# Revit family: IS_Conca_T3971_BIM_IT
name_source: partatom
category: Plumbing Fixtures
revit_build: Autodesk Revit 2017 (Build: 20160225_1515(x64)
units: mm (PartAtom-declared; Revit-internal decimal feet)

## family parameters
Always vertical = No
Cut with Voids When Loaded = No
OmniClass Number = 23.45.05.14.21.11
OmniClass Title = Bath/Shower Units
Part Type = Normal
Room Calculation Point = No
Round Connector Dimension = Use Diameter
Shared = No
Work Plane-Based = No

## types (3) — shared parameters
BIMobject category = Storage
BIMobject category code = sanitary-storage
BIMobject main category = Sanitary
BIMobject main category code = sanitary
Installation instructions = https://www.idealspec.co.uk
Maniglia = No
Manufacturer = Ideal Standard
NominalDepth = 505 mm  [stored 1.65682 ft]
NominalHeight = 6 mm  [stored 0.019685 ft]
NominalWidth = 1001 mm  [stored 3.28412 ft]
PiattoDoccia = No
Product group = Bathroom_Furniture
URL = https://www.ideal-standard.co.uk
Uniclass 2015 Code = Pr_40_30_78_03
Uniclass 2015 Name = Bathroom cabinets
zero-valued in all types: CostoDiSostituzione, DimensioneScarico, LunghezzaNominale, Nominal depth, Nominal height, SeatMaterial, SpessoreDelMateriale, SpilloverLivello, Weight Net (Kg)

## per-type parameters (varying)
- T3971DG - Conca CERAMIC WTOP 100 X 50.5  CM BLM - T3971 - DG: AltezzaNominale=0 mm  [stored 0 ft]; Description=Porcelain stoneware countertop,   1200 x 505 x 6 mm . Compact, hard non-porous colored ceramic with high resistance to mechanical stress, chemical attack, scratches and abrasion. It is easy to clean. To be combined with vanity units without countertop.Black Marble finish.; LarghezzaNominale=0 mm  [stored 0 ft]; Model=T3971DG; ProfonditaNominale=0 mm  [stored 0 ft]
- T3971DH - Conca CERAMIC WTOP 100 X 50.5  CM BLM - T3971 - DH: AltezzaNominale=0 mm  [stored 0 ft]; Description=Porcelain stoneware countertop,   1200 x 505 x 6 mm . Compact, hard non-porous colored ceramic with high resistance to mechanical stress, chemical attack, scratches and abrasion. It is easy to clean. To be combined with vanity units without countertop.Black Marble finish.; LarghezzaNominale=0 mm  [stored 0 ft]; Model=T3971DG; ProfonditaNominale=0 mm  [stored 0 ft]
- T3971DI - Conca CERAMIC WTOP 100 X 50.5  CM BLM - T3971 - DI: Accessori=https://www.idealstandard.it; Aiuto=https://www.idealstandard.it; AltezzaNominale=6 mm  [stored 0.019685 ft]; Autore=Ideal Standard; Brand=https://www.idealstandard.it; Caratteristiche=Piano da appogio in gres porcellanato  1200 x 505 x 6 mm  Il gres porcellanato è una ceramica a pasta compatta e dura colorata non porosa un'elevata resistenza alle sollecitazioni meccaniche, agli attacchi chimici, ai graffi e all'abrasione. Si pulisce con estrema facilità. Da abbinare ai mobili sottolavabo senza piano da appoggio.Finitura Marmo nero lucido; CodiceABarre=8014140461951; CodiceArticolo=T3971DI; Colore=Black Marble finish.; Description=Porcelain stoneware countertop,   1200 x 505 x 6 mm . Compact, hard non-porous colored ceramic with high resistance to mechanical stress, chemical attack, scratches and abrasion. It is easy to clean. To be combined with vanity units without countertop. Polished black marble finish; DescrizioneClassifcazioneUni2015=Bathroom cabinets; Desrizione=Piano da appogio in gres porcellanato  1200 x 505 x 6 mm  Il gres porcellanato è una ceramica a pasta compatta e dura colorata non porosa un'elevata resistenza alle sollecitazioni meccaniche, agli attacchi chimici, ai graffi e all'abrasione. Si pulisce con estrema facilità. Da abbinare ai mobili sottolavabo senza piano da appoggio.Finitura Marmo nero lucido; DurataGaranzia=2; DurataGaranziaProdotti=2; Finitura=Black Marble finish.; Forma=Rettangolare; Garanzia=Garanzia Idealstandard; IfcEsportaCome=IfcFurnitureType; InformaziniGaranzia=https://www.idealstandard.it; InformazioniDiProdotto=http://www.idealstandard.it; InformazioniGaranzia=https://www.idealstandard.it; InstruzioniInstallazione=https://www.idealstandard.it; LarghezzaNominale=1003 mm; Materiale=Ceramics; Model=T3971DI; ModelloDiRiferimento=T3971DI; Nome=BathroomCabinets_Conca_T3971DI_IdealStandard; NomeOggettoBim=ISI_IdealStandard_Bathroom Cabinets_Conca_T3971DI; NumeroDiModello=T3971DI; PesoNetto=7; Produttore=Ideal Standard; ProfonditaNominale=505 mm  [stored 1.65682 ft]; Revisione=1; RiferimentoClassificazioneUni2015=Pr_40_30_78_03; Spazio=Interno; Telefono=800 652 290; TipoEspotazioneIfc=Bathroom cabinets; UnitàDurata=Anno; UnitàDurataGaranzia=Anno; UnitàLineare=Milimitre; UnitàMonetaria=€; UnitàSuperficie=Milimitre; UnitàVolume=Litri; Versione=1; VersioneClassificazioneUni2015=v1.1

note: [stored X ft] marks values corroborated as IEEE doubles in the binary element streams (Revit-internal decimal feet)

## geometry (parser evidence)
native form markers: Sweep x3
no freeform markers — native parametric forms only
